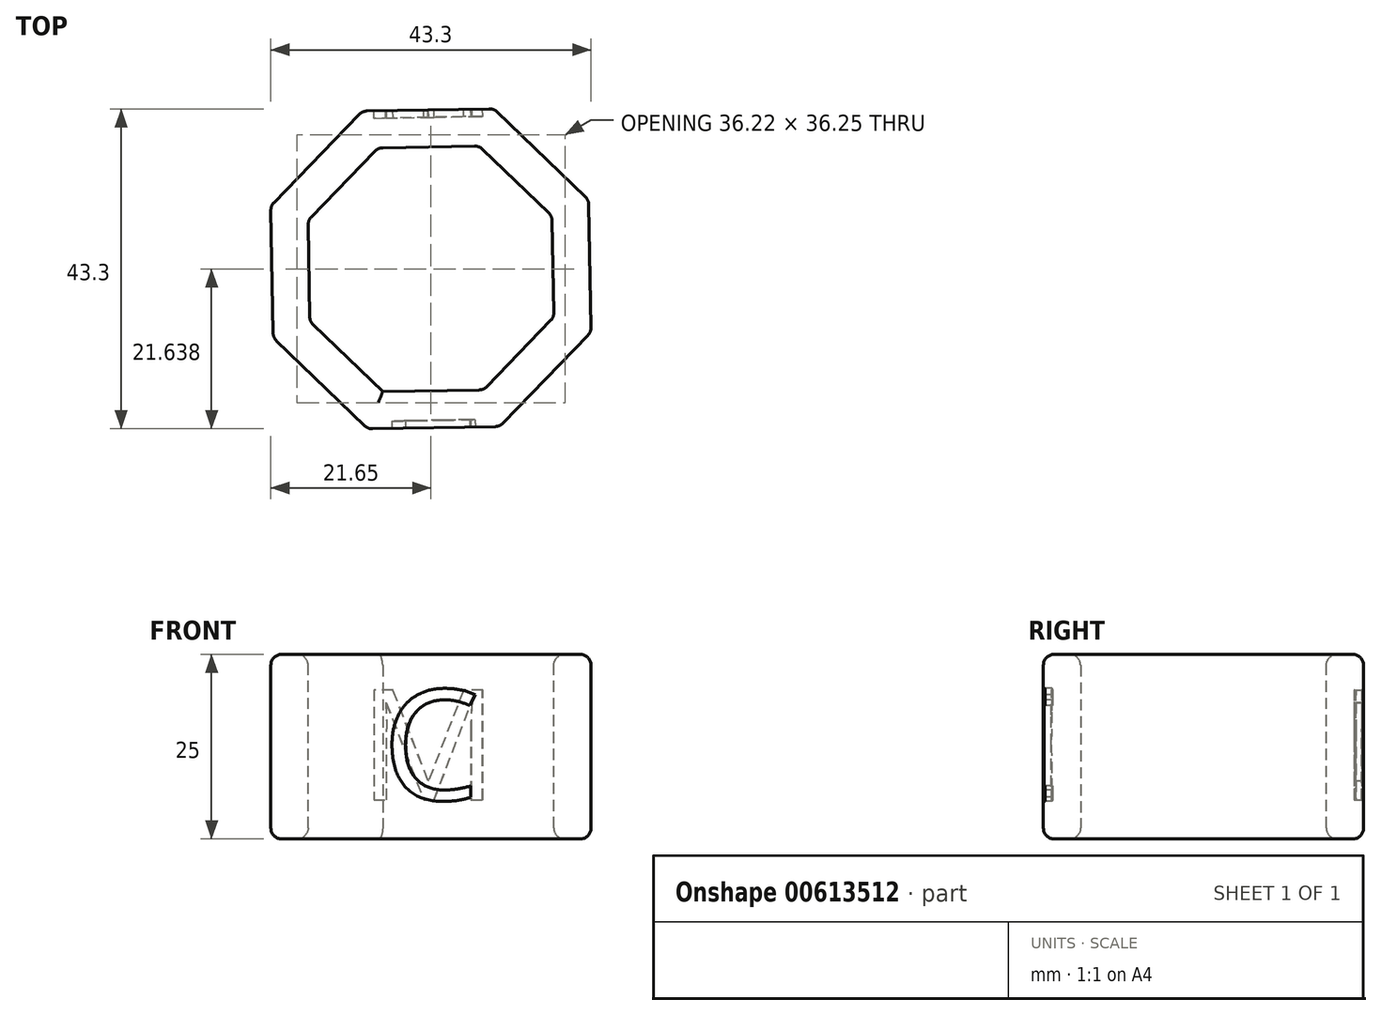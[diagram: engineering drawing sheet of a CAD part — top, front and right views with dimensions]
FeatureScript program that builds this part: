
annotation { "Feature Type Name" : "Feature", "Feature Type Description" : "" }
export const myFeature = defineFeature(function(context is Context, id is Id, definition is map)
    precondition{}
    {
        {
            var Q0;
            Q0=qCreatedBy(makeId("Top.planeOp"),FACE);
            var sketch = newSketch(context, id + "F0", { "sketchPlane" : qUnion([Q0])});
            skCircle(sketch, "E0.cCircle", {"center": v(0, 0) * mm, "radius": 16.5 * mm, "construction": true});
            skLineSegment(sketch, "E0.0", {"start": v(6.53, 16.62) * mm, "end": v(16.37, 7.14) * mm});
            skLineSegment(sketch, "E0.1", {"start": v(16.37, 7.14) * mm, "end": v(16.62, -6.53) * mm});
            skLineSegment(sketch, "E0.2", {"start": v(16.62, -6.53) * mm, "end": v(7.14, -16.37) * mm});
            skLineSegment(sketch, "E0.3", {"start": v(7.14, -16.37) * mm, "end": v(-6.53, -16.62) * mm});
            skLineSegment(sketch, "E0.4", {"start": v(-6.53, -16.62) * mm, "end": v(-16.37, -7.14) * mm});
            skLineSegment(sketch, "E0.5", {"start": v(-16.37, -7.14) * mm, "end": v(-16.62, 6.53) * mm});
            skLineSegment(sketch, "E0.6", {"start": v(-16.62, 6.53) * mm, "end": v(-7.14, 16.37) * mm});
            skLineSegment(sketch, "E0.7", {"start": v(-7.14, 16.37) * mm, "end": v(6.53, 16.62) * mm});
            skPoint(sketch, "E0.0.midPoint", {"position": v(11.45, 11.88) * mm});
            skLineSegment(sketch, "E1.0", {"start": v(-21.66, 8.5) * mm, "end": v(-9.3, 21.33) * mm});
            skLineSegment(sketch, "E1.1", {"start": v(-21.33, -9.3) * mm, "end": v(-21.66, 8.5) * mm});
            skLineSegment(sketch, "E1.2", {"start": v(-9.3, 21.33) * mm, "end": v(8.5, 21.66) * mm});
            skLineSegment(sketch, "E1.3", {"start": v(-8.5, -21.66) * mm, "end": v(-21.33, -9.3) * mm});
            skLineSegment(sketch, "E1.4", {"start": v(8.5, 21.66) * mm, "end": v(21.33, 9.3) * mm});
            skLineSegment(sketch, "E1.5", {"start": v(21.33, 9.3) * mm, "end": v(21.66, -8.5) * mm});
            skLineSegment(sketch, "E1.6", {"start": v(21.66, -8.5) * mm, "end": v(9.3, -21.33) * mm});
            skLineSegment(sketch, "E1.7", {"start": v(9.3, -21.33) * mm, "end": v(-8.5, -21.66) * mm});
            skSolve(sketch);
        }
        {
            var Q0;
            Q0=makeQuery(id+"F0.imprint","IMPRINT",FACE,{"disambiguationData":[TD([[makeQuery(id+"F0.imprint","IMPRINT",EDGE,{"derivedFrom":sQuery(id+"F0.wireOp",EDGE,"E0.0")}),1.0]])]});
            extrude(context, id + "F1", {"entities" : qUnion([Q0]), "depth" : 25 * mm, "offsetDistance" : 25 * mm});
        }
        {
            var Q0;
            Q0=makeQuery(id+"F1.opExtrude","SWEPT_EDGE",EDGE,{"disambiguationData":[OSD([sQuery(id+"F0.wireOp",EDGE,"E1.3"),sQuery(id+"F0.wireOp",EDGE,"E1.7")])]});
            var Q1;
            Q1=makeQuery(id+"F1.opExtrude","SWEPT_EDGE",EDGE,{"disambiguationData":[OSD([sQuery(id+"F0.wireOp",EDGE,"E1.6"),sQuery(id+"F0.wireOp",EDGE,"E1.7")])]});
            var Q2;
            Q2=makeQuery(id+"F1.opExtrude","CAP_EDGE",EDGE,{"disambiguationData":[OSD([sQuery(id+"F0.wireOp",EDGE,"E1.6")])],"isStart":false});
            var Q3;
            Q3=makeQuery(id+"F1.opExtrude","CAP_EDGE",EDGE,{"disambiguationData":[OSD([sQuery(id+"F0.wireOp",EDGE,"E1.7")])],"isStart":false});
            var Q4;
            Q4=makeQuery(id+"F1.opExtrude","CAP_EDGE",EDGE,{"disambiguationData":[OSD([sQuery(id+"F0.wireOp",EDGE,"E1.3")])],"isStart":false});
            var Q5;
            Q5=makeQuery(id+"F1.opExtrude","CAP_EDGE",EDGE,{"disambiguationData":[OSD([sQuery(id+"F0.wireOp",EDGE,"E1.1")])],"isStart":false});
            var Q6;
            Q6=makeQuery(id+"F1.opExtrude","CAP_EDGE",EDGE,{"disambiguationData":[OSD([sQuery(id+"F0.wireOp",EDGE,"E1.0")])],"isStart":false});
            var Q7;
            Q7=makeQuery(id+"F1.opExtrude","CAP_EDGE",EDGE,{"disambiguationData":[OSD([sQuery(id+"F0.wireOp",EDGE,"E1.2")])],"isStart":false});
            var Q8;
            Q8=makeQuery(id+"F1.opExtrude","CAP_EDGE",EDGE,{"disambiguationData":[OSD([sQuery(id+"F0.wireOp",EDGE,"E1.4")])],"isStart":false});
            var Q9;
            Q9=makeQuery(id+"F1.opExtrude","CAP_EDGE",EDGE,{"disambiguationData":[OSD([sQuery(id+"F0.wireOp",EDGE,"E1.5")])],"isStart":false});
            var Q10;
            Q10=makeQuery(id+"F1.opExtrude","SWEPT_EDGE",EDGE,{"disambiguationData":[OSD([sQuery(id+"F0.wireOp",EDGE,"E1.5"),sQuery(id+"F0.wireOp",EDGE,"E1.6")])]});
            var Q11;
            Q11=makeQuery(id+"F1.opExtrude","SWEPT_EDGE",EDGE,{"disambiguationData":[OSD([sQuery(id+"F0.wireOp",EDGE,"E1.1"),sQuery(id+"F0.wireOp",EDGE,"E1.3")])]});
            var Q12;
            Q12=makeQuery(id+"F1.opExtrude","SWEPT_EDGE",EDGE,{"disambiguationData":[OSD([sQuery(id+"F0.wireOp",EDGE,"E1.0"),sQuery(id+"F0.wireOp",EDGE,"E1.1")])]});
            var Q13;
            Q13=makeQuery(id+"F1.opExtrude","SWEPT_EDGE",EDGE,{"disambiguationData":[OSD([sQuery(id+"F0.wireOp",EDGE,"E1.0"),sQuery(id+"F0.wireOp",EDGE,"E1.2")])]});
            var Q14;
            Q14=makeQuery(id+"F1.opExtrude","SWEPT_EDGE",EDGE,{"disambiguationData":[OSD([sQuery(id+"F0.wireOp",EDGE,"E1.4"),sQuery(id+"F0.wireOp",EDGE,"E1.5")])]});
            var Q15;
            Q15=makeQuery(id+"F1.opExtrude","CAP_EDGE",EDGE,{"disambiguationData":[OSD([sQuery(id+"F0.wireOp",EDGE,"E1.5")])],"isStart":true});
            var Q16;
            Q16=makeQuery(id+"F1.opExtrude","CAP_EDGE",EDGE,{"disambiguationData":[OSD([sQuery(id+"F0.wireOp",EDGE,"E1.6")])],"isStart":true});
            var Q17;
            Q17=makeQuery(id+"F1.opExtrude","CAP_EDGE",EDGE,{"disambiguationData":[OSD([sQuery(id+"F0.wireOp",EDGE,"E1.7")])],"isStart":true});
            var Q18;
            Q18=makeQuery(id+"F1.opExtrude","CAP_EDGE",EDGE,{"disambiguationData":[OSD([sQuery(id+"F0.wireOp",EDGE,"E1.3")])],"isStart":true});
            var Q19;
            Q19=makeQuery(id+"F1.opExtrude","CAP_EDGE",EDGE,{"disambiguationData":[OSD([sQuery(id+"F0.wireOp",EDGE,"E0.5")])],"isStart":true});
            var Q20;
            Q20=makeQuery(id+"F1.opExtrude","CAP_EDGE",EDGE,{"disambiguationData":[OSD([sQuery(id+"F0.wireOp",EDGE,"E1.0")])],"isStart":true});
            var Q21;
            Q21=makeQuery(id+"F1.opExtrude","CAP_EDGE",EDGE,{"disambiguationData":[OSD([sQuery(id+"F0.wireOp",EDGE,"E1.1")])],"isStart":true});
            var Q22;
            Q22=makeQuery(id+"F1.opExtrude","CAP_EDGE",EDGE,{"disambiguationData":[OSD([sQuery(id+"F0.wireOp",EDGE,"E0.4")])],"isStart":true});
            var Q23;
            Q23=makeQuery(id+"F1.opExtrude","CAP_EDGE",EDGE,{"disambiguationData":[OSD([sQuery(id+"F0.wireOp",EDGE,"E0.3")])],"isStart":true});
            var Q24;
            Q24=makeQuery(id+"F1.opExtrude","CAP_EDGE",EDGE,{"disambiguationData":[OSD([sQuery(id+"F0.wireOp",EDGE,"E0.2")])],"isStart":true});
            var Q25;
            Q25=makeQuery(id+"F1.opExtrude","CAP_EDGE",EDGE,{"disambiguationData":[OSD([sQuery(id+"F0.wireOp",EDGE,"E0.1")])],"isStart":true});
            var Q26;
            Q26=makeQuery(id+"F1.opExtrude","CAP_EDGE",EDGE,{"disambiguationData":[OSD([sQuery(id+"F0.wireOp",EDGE,"E0.0")])],"isStart":true});
            var Q27;
            Q27=makeQuery(id+"F1.opExtrude","CAP_EDGE",EDGE,{"disambiguationData":[OSD([sQuery(id+"F0.wireOp",EDGE,"E0.7")])],"isStart":true});
            var Q28;
            Q28=makeQuery(id+"F1.opExtrude","CAP_EDGE",EDGE,{"disambiguationData":[OSD([sQuery(id+"F0.wireOp",EDGE,"E0.6")])],"isStart":true});
            var Q29;
            Q29=makeQuery(id+"F1.opExtrude","SWEPT_EDGE",EDGE,{"disambiguationData":[OSD([sQuery(id+"F0.wireOp",EDGE,"E1.2"),sQuery(id+"F0.wireOp",EDGE,"E1.4")])]});
            var Q30;
            Q30=makeQuery(id+"F1.opExtrude","SWEPT_EDGE",EDGE,{"disambiguationData":[OSD([sQuery(id+"F0.wireOp",EDGE,"E0.2"),sQuery(id+"F0.wireOp",EDGE,"E0.3")])]});
            var Q31;
            Q31=makeQuery(id+"F1.opExtrude","SWEPT_EDGE",EDGE,{"disambiguationData":[OSD([sQuery(id+"F0.wireOp",EDGE,"E0.4"),sQuery(id+"F0.wireOp",EDGE,"E0.5")])]});
            var Q32;
            Q32=makeQuery(id+"F1.opExtrude","CAP_EDGE",EDGE,{"disambiguationData":[OSD([sQuery(id+"F0.wireOp",EDGE,"E0.6")])],"isStart":false});
            var Q33;
            Q33=makeQuery(id+"F1.opExtrude","SWEPT_EDGE",EDGE,{"disambiguationData":[OSD([sQuery(id+"F0.wireOp",EDGE,"E0.5"),sQuery(id+"F0.wireOp",EDGE,"E0.6")])]});
            var Q34;
            Q34=makeQuery(id+"F1.opExtrude","CAP_EDGE",EDGE,{"disambiguationData":[OSD([sQuery(id+"F0.wireOp",EDGE,"E0.5")])],"isStart":false});
            var Q35;
            Q35=makeQuery(id+"F1.opExtrude","CAP_EDGE",EDGE,{"disambiguationData":[OSD([sQuery(id+"F0.wireOp",EDGE,"E0.4")])],"isStart":false});
            var Q36;
            Q36=makeQuery(id+"F1.opExtrude","SWEPT_EDGE",EDGE,{"disambiguationData":[OSD([sQuery(id+"F0.wireOp",EDGE,"E0.0"),sQuery(id+"F0.wireOp",EDGE,"E0.1")])]});
            var Q37;
            Q37=makeQuery(id+"F1.opExtrude","SWEPT_FACE",FACE,{"disambiguationData":[OSD([sQuery(id+"F0.wireOp",EDGE,"E0.1")])]});
            var Q38;
            Q38=makeQuery(id+"F1.opExtrude","SWEPT_EDGE",EDGE,{"disambiguationData":[OSD([sQuery(id+"F0.wireOp",EDGE,"E0.1"),sQuery(id+"F0.wireOp",EDGE,"E0.2")])]});
            var Q39;
            Q39=makeQuery(id+"F1.opExtrude","CAP_EDGE",EDGE,{"disambiguationData":[OSD([sQuery(id+"F0.wireOp",EDGE,"E0.3")])],"isStart":false});
            var Q40;
            Q40=makeQuery(id+"F1.opExtrude","CAP_EDGE",EDGE,{"disambiguationData":[OSD([sQuery(id+"F0.wireOp",EDGE,"E1.2")])],"isStart":true});
            var Q41;
            Q41=makeQuery(id+"F1.opExtrude","CAP_EDGE",EDGE,{"disambiguationData":[OSD([sQuery(id+"F0.wireOp",EDGE,"E1.4")])],"isStart":true});
            var Q42;
            Q42=makeQuery(id+"F1.opExtrude","CAP_EDGE",EDGE,{"disambiguationData":[OSD([sQuery(id+"F0.wireOp",EDGE,"E0.0")])],"isStart":false});
            var Q43;
            Q43=makeQuery(id+"F1.opExtrude","SWEPT_EDGE",EDGE,{"disambiguationData":[OSD([sQuery(id+"F0.wireOp",EDGE,"E0.0"),sQuery(id+"F0.wireOp",EDGE,"E0.7")])]});
            var Q44;
            Q44=makeQuery(id+"F1.opExtrude","CAP_EDGE",EDGE,{"disambiguationData":[OSD([sQuery(id+"F0.wireOp",EDGE,"E0.7")])],"isStart":false});
            var Q45;
            Q45=makeQuery(id+"F1.opExtrude","SWEPT_EDGE",EDGE,{"disambiguationData":[OSD([sQuery(id+"F0.wireOp",EDGE,"E0.6"),sQuery(id+"F0.wireOp",EDGE,"E0.7")])]});
            var Q46;
            Q46=makeQuery(id+"F1.opExtrude","CAP_EDGE",EDGE,{"disambiguationData":[OSD([sQuery(id+"F0.wireOp",EDGE,"E0.2")])],"isStart":false});
            var Q47;
            Q47=makeQuery(id+"F1.opExtrude","CAP_EDGE",EDGE,{"disambiguationData":[OSD([sQuery(id+"F0.wireOp",EDGE,"E0.1")])],"isStart":false});
            fillet(context, id + "F2", {"entities" : qUnion([Q0, Q1, Q2, Q3, Q4, Q5, Q6, Q7, Q8, Q9, Q10, Q11, Q12, Q13, Q14, Q15, Q16, Q17, Q18, Q19, Q20, Q21, Q22, Q23, Q24, Q25, Q26, Q27, Q28, Q29, Q30, Q31, Q32, Q33, Q34, Q35, Q36, Q37, Q38, Q39, Q40, Q41, Q42, Q43, Q44, Q45, Q46, Q47]), "radius" : 1.5 * mm, "tangentPropagation" : true, "allowEdgeOverflow" : false});
        }
        {
            var Q0;
            Q0=makeQuery(id+"F1.opExtrude","SWEPT_FACE",FACE,{"disambiguationData":[OSD([sQuery(id+"F0.wireOp",EDGE,"E1.7")])]});
            var sketch = newSketch(context, id + "F3", { "sketchPlane" : qUnion([Q0])});
            skText(sketch, "E2", { "text": "C", "fontName": "OpenSans-Regular.ttf"});
            const initialGuessF3  = {"E2": [-0.00694, 0.0053, 1, 0, 0.015]};
            skSetInitialGuess(sketch, initialGuessF3);
            skSolve(sketch);
        }
        {
            var Q0;
            Q0 = qSketchRegion(id + "F3", true);
            extrude(context, id + "F4", {"entities" : qUnion([Q0]), "operationType" : NewBodyOperationType.REMOVE, "oppositeDirection" : true, "depth" : 1 * mm, "offsetDistance" : 25 * mm});
        }
        {
            var Q0;
            Q0=makeQuery(id+"F1.opExtrude","SWEPT_FACE",FACE,{"disambiguationData":[OSD([sQuery(id+"F0.wireOp",EDGE,"E1.2")])]});
            var sketch = newSketch(context, id + "F5", { "sketchPlane" : qUnion([Q0])});
            skText(sketch, "E3", { "text": "M", "fontName": "OpenSans-Regular.ttf"});
            const initialGuessF5  = {"E3": [-0.00944, 0.0053, 1, 0, 0.015]};
            skSetInitialGuess(sketch, initialGuessF5);
            skSolve(sketch);
        }
        {
            var Q0;
            Q0 = qSketchRegion(id + "F5", true);
            extrude(context, id + "F6", {"entities" : qUnion([Q0]), "operationType" : NewBodyOperationType.REMOVE, "oppositeDirection" : true, "depth" : 1 * mm, "offsetDistance" : 25 * mm});
        }
    });
